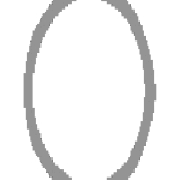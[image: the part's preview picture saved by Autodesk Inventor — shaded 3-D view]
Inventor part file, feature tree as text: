
AUTODESK INVENTOR PART (.ipt)
format: ipt  version: 2021 (Build 250183000, 183)  size: 109,568 bytes
history: native  units: in
note: dims shown in document units (in); Inventor stores cm internally (conversion verified against a paired STEP export)
features: other x4, sketch x3, plane x1
ambient origin geometry x8: Origin, YZ Plane, XZ Plane, XY Plane, X Axis, Y Axis, Z Axis, Center Point
bodies: Solid1 (feature_tree), Body (feature_tree)
feature tree (8):
  other  "Driven Length"
  other  "Frame Generator"
  other  "Start Plane"
  other  "End Plane"
  sketch  "Sketch"  dims[d2=21.1542in d4=-0.0in d5=21.1542in d6=0.12in d7=0.0in d8=90.0deg d9=21.1542in]
  sketch  "Sketch2"  dims[d0=1.0in]
  plane  "Work Plane3"
  sketch  "Sketch3"  dims[d1=0.065in]
